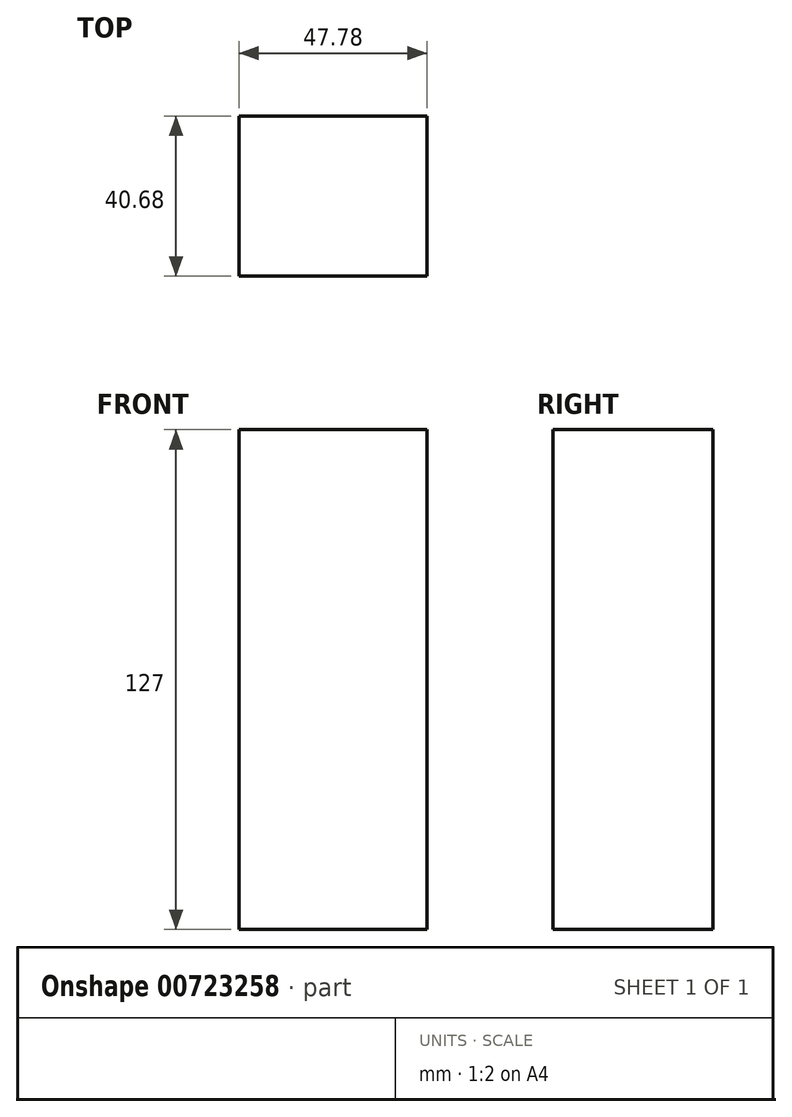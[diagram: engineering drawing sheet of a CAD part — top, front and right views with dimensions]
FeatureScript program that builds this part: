
annotation { "Feature Type Name" : "Feature", "Feature Type Description" : "" }
export const myFeature = defineFeature(function(context is Context, id is Id, definition is map)
    precondition{}
    {
        {
            var Q0;
            Q0=qCreatedBy(makeId("Top.planeOp"),FACE);
            var sketch = newSketch(context, id + "F0", { "sketchPlane" : qUnion([Q0])});
            skLineSegment(sketch, "E0.bottom", {"start": v(23.9, 20.34) * mm, "end": v(-23.9, 20.34) * mm});
            skLineSegment(sketch, "E0.top", {"start": v(23.9, -20.34) * mm, "end": v(-23.9, -20.34) * mm});
            skLineSegment(sketch, "E0.left", {"start": v(23.9, 20.34) * mm, "end": v(23.9, -20.34) * mm});
            skLineSegment(sketch, "E0.right", {"start": v(-23.9, 20.34) * mm, "end": v(-23.9, -20.34) * mm});
            skPoint(sketch, "E0.middle", {"position": v(0, 0) * mm});
            skSolve(sketch);
        }
        {
            var Q0;
            Q0=makeQuery(id+"F0.imprint","IMPRINT",FACE,{"disambiguationData":[TD([[makeQuery(id+"F0.imprint","IMPRINT",EDGE,{"derivedFrom":sQuery(id+"F0.wireOp",EDGE,"E0.bottom")}),1.0]])]});
            extrude(context, id + "F1", {"entities" : qUnion([Q0]), "depth" : 127 * mm, "offsetDistance" : 25.4 * mm});
        }
    });
